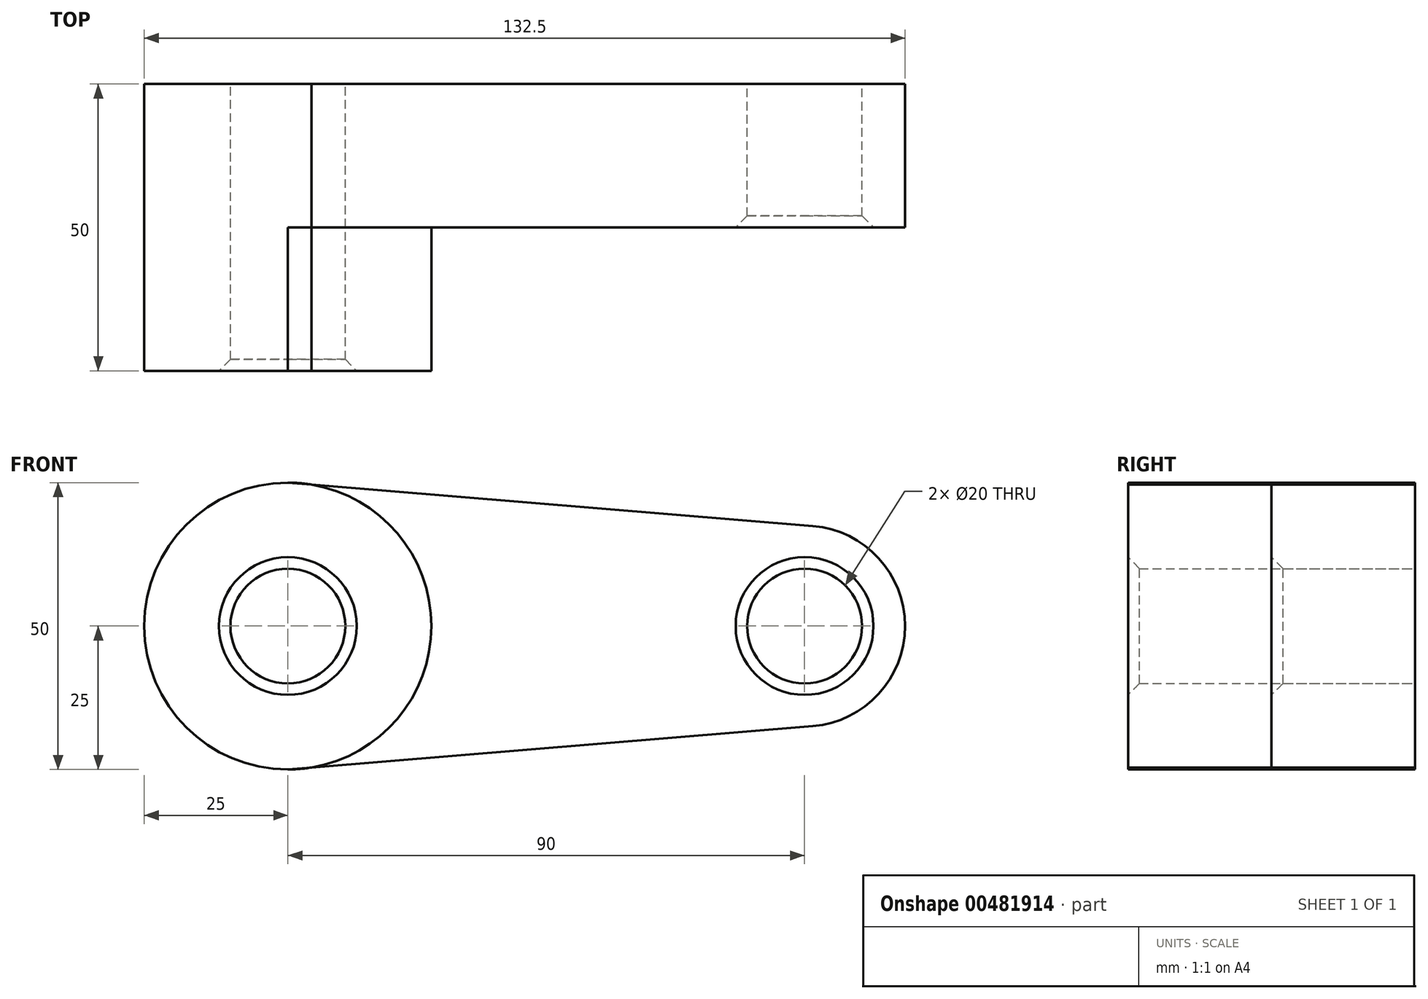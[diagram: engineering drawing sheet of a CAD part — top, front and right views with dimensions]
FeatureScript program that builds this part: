
annotation { "Feature Type Name" : "Feature", "Feature Type Description" : "" }
export const myFeature = defineFeature(function(context is Context, id is Id, definition is map)
    precondition{}
    {
        {
            var Q0;
            Q0=qCreatedBy(makeId("Front.planeOp"),FACE);
            var sketch = newSketch(context, id + "F0", { "sketchPlane" : qUnion([Q0])});
            skCircle(sketch, "E0", {"center": v(0, 0) * mm, "radius": 25 * mm});
            skCircle(sketch, "E1", {"center": v(90, 0) * mm, "radius": 17.5 * mm});
            skLineSegment(sketch, "E2", {"start": v(0, 25) * mm, "end": v(91.44, 17.44) * mm});
            skLineSegment(sketch, "E3", {"start": v(0, -25) * mm, "end": v(91.44, -17.44) * mm});
            skCircle(sketch, "E4", {"center": v(0, 0) * mm, "radius": 10 * mm});
            skCircle(sketch, "E5", {"center": v(90, 0) * mm, "radius": 10 * mm});
            skSolve(sketch);
        }
        {
            var Q0;
            Q0 = qSketchRegion(id + "F0", true);
            extrude(context, id + "F1", {"entities" : qUnion([Q0]), "depth" : 25 * mm});
        }
        {
            var Q0;
            Q0=makeQuery(id+"F0.imprint","IMPRINT",FACE,{"disambiguationData":[TD([[makeQuery(id+"F0.imprint","IMPRINT",EDGE,{"derivedFrom":sQuery(id+"F0.wireOp",EDGE,"E4")}),-1.0]])]});
            extrude(context, id + "F2", {"entities" : qUnion([Q0]), "operationType" : NewBodyOperationType.ADD, "depth" : 50 * mm});
        }
        {
            var Q0;
            Q0=makeQuery(id+"F2.opExtrude","CAP_EDGE",EDGE,{"disambiguationData":[OSD([sQuery(id+"F0.wireOp",EDGE,"E4")])],"isStart":false});
            var Q1;
            {var subQ0=sQuery(id+"F0.wireOp",EDGE,"E0");Q1=makeQuery(id+"F2.opExtrude","CAP_EDGE",EDGE,{"disambiguationData":[OSD([subQ0]),TDD([makeQuery(id+"F0.imprint","IMPRINT",EDGE,{"disambiguationData":[TD([[makeQuery(id+"F0.imprint","INTERSECT",VERTEX,{"disambiguationData":[OD(0.0)],"derivedFrom":[subQ0,sQuery(id+"F0.wireOp",EDGE,"E2")]}),-1.0]])],"derivedFrom":subQ0})])],"isStart":false});}
            var Q2;
            Q2=makeQuery(id+"F1.opExtrude","CAP_EDGE",EDGE,{"disambiguationData":[OSD([sQuery(id+"F0.wireOp",EDGE,"E5")])],"isStart":false});
            chamfer(context, id + "F3", {"entities" : qUnion([Q0, Q1, Q2]), "width" : 2 * mm, "tangentPropagation" : true});
        }
    });
